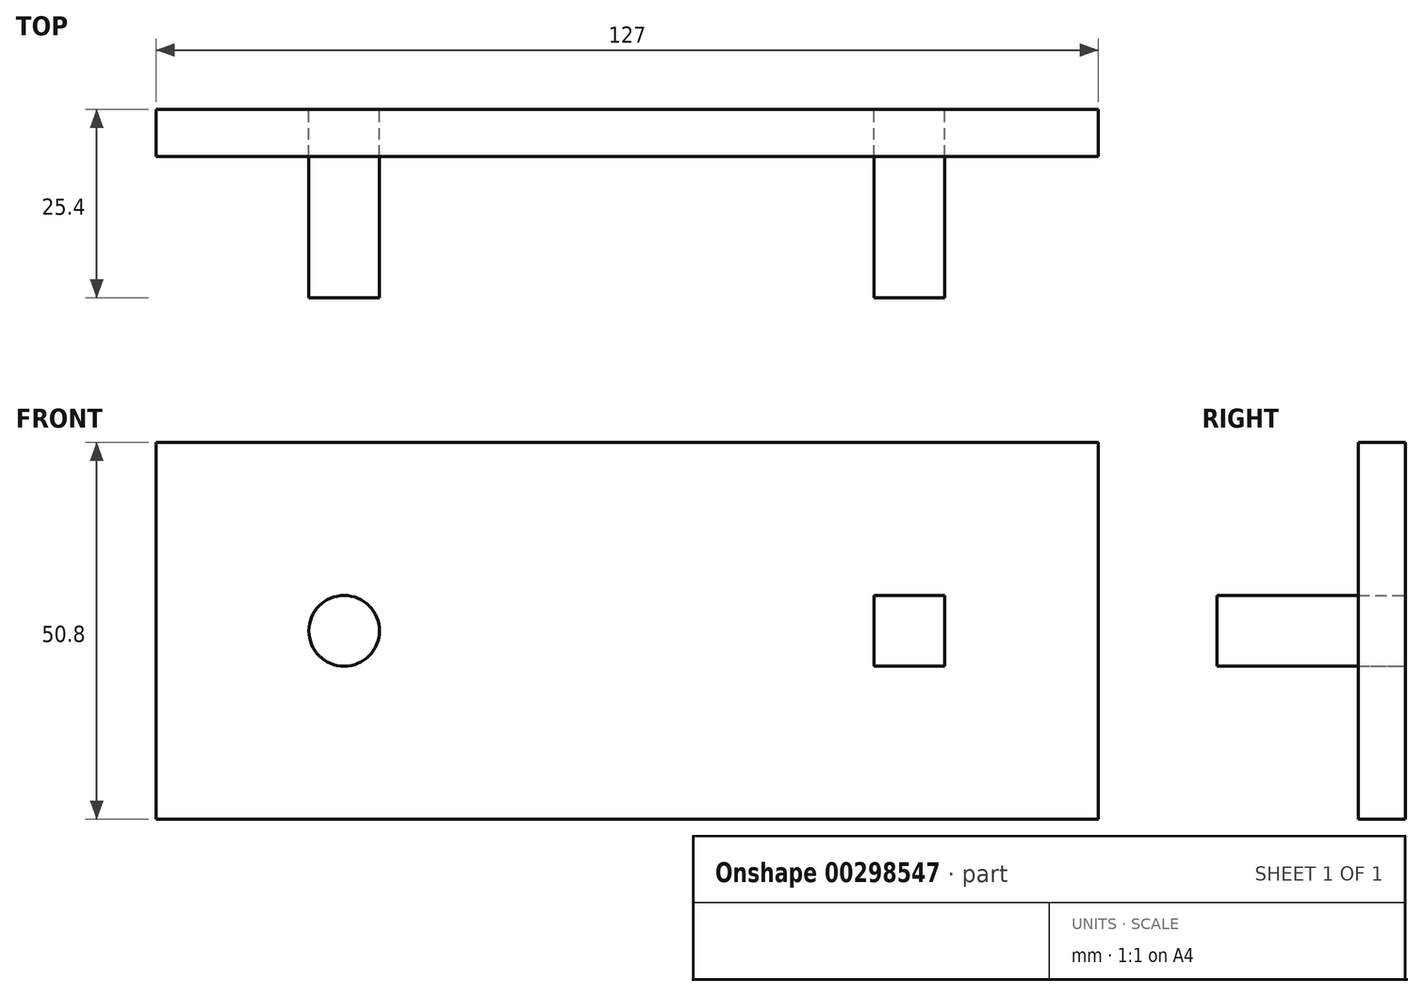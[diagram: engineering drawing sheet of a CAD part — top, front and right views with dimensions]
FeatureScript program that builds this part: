
annotation { "Feature Type Name" : "Feature", "Feature Type Description" : "" }
export const myFeature = defineFeature(function(context is Context, id is Id, definition is map)
    precondition{}
    {
        {
            var Q0;
            Q0=qCreatedBy(makeId("Front.planeOp"),FACE);
            var sketch = newSketch(context, id + "F0", { "sketchPlane" : qUnion([Q0])});
            skLineSegment(sketch, "E0.bottom", {"start": v(63.5, 25.4) * mm, "end": v(-63.5, 25.4) * mm});
            skLineSegment(sketch, "E0.top", {"start": v(63.5, -25.4) * mm, "end": v(-63.5, -25.4) * mm});
            skLineSegment(sketch, "E0.left", {"start": v(63.5, 25.4) * mm, "end": v(63.5, -25.4) * mm});
            skLineSegment(sketch, "E0.right", {"start": v(-63.5, 25.4) * mm, "end": v(-63.5, -25.4) * mm});
            skPoint(sketch, "E0.middle", {"position": v(0, 0) * mm});
            skSolve(sketch);
        }
        {
            var Q0;
            Q0=qCreatedBy(makeId("Front.planeOp"),FACE);
            var sketch = newSketch(context, id + "F1", { "sketchPlane" : qUnion([Q0])});
            skCircle(sketch, "E1", {"center": v(-38.15, 0) * mm, "radius": 4.76 * mm});
            skLineSegment(sketch, "E2.bottom", {"start": v(42.81, 4.76) * mm, "end": v(33.29, 4.76) * mm});
            skLineSegment(sketch, "E2.top", {"start": v(42.81, -4.76) * mm, "end": v(33.29, -4.76) * mm});
            skLineSegment(sketch, "E2.left", {"start": v(42.81, 4.76) * mm, "end": v(42.81, -4.76) * mm});
            skLineSegment(sketch, "E2.right", {"start": v(33.29, 4.76) * mm, "end": v(33.29, -4.76) * mm});
            skPoint(sketch, "E2.middle", {"position": v(38.05, 0) * mm});
            skSolve(sketch);
        }
        {
            var Q0;
            {var subQ0=sQuery(id+"F1.wireOp",EDGE,"5Zl7hWcx-Vfif-6HsS-f2ZM-u7ULnNQ5xVKX");var subQ1=sQuery(id+"F1.wireOp",EDGE,"ShflypP2-Z43F-BW97-jndV-6qC142foT7Cp");var subQ2=makeQuery(id+"F1.imprint","INTERSECT",VERTEX,{"derivedFrom":[subQ1,subQ0]});Q0=makeQuery(id+"F1.imprint","IMPRINT",FACE,{"disambiguationData":[TD([[makeQuery(id+"F1.imprint","IMPRINT",EDGE,{"disambiguationData":[TD([[subQ2,1.0]])],"derivedFrom":subQ1}),-1.0]])]});}
            var Q1;
            {var subQ0=sQuery(id+"F1.wireOp",EDGE,"5Zl7hWcx-Vfif-6HsS-f2ZM-u7ULnNQ5xVKX");var subQ1=sQuery(id+"F1.wireOp",EDGE,"ShflypP2-Z43F-BW97-jndV-6qC142foT7Cp");var subQ2=makeQuery(id+"F1.imprint","INTERSECT",VERTEX,{"derivedFrom":[subQ1,subQ0]});Q1=makeQuery(id+"F1.imprint","IMPRINT",FACE,{"disambiguationData":[TD([[makeQuery(id+"F1.imprint","IMPRINT",EDGE,{"disambiguationData":[TD([[subQ2,1.0]])],"derivedFrom":subQ1}),1.0]])]});}
            var Q2;
            {var subQ1=sQuery(id+"F1.wireOp",EDGE,"E2.bottom");Q2=makeQuery(id+"F1.imprint","IMPRINT",FACE,{"disambiguationData":[TD([[makeQuery(id+"F1.imprint","IMPRINT",EDGE,{"derivedFrom":subQ1}),1.0]])]});}
            var Q3;
            Q3=makeQuery(id+"F0.imprint","IMPRINT",FACE,{"disambiguationData":[TD([[makeQuery(id+"F0.imprint","IMPRINT",EDGE,{"derivedFrom":sQuery(id+"F0.wireOp",EDGE,"E0.bottom")}),1.0]])]});
            extrude(context, id + "F2", {"entities" : qUnion([Q0, Q1, Q2, Q3]), "depth" : 6.35 * mm});
        }
        {
            var Q0;
            Q0=qSketchRegion(id+"F1",true);
            extrude(context, id + "F3", {"entities" : qUnion([Q0]), "depth" : 25.4 * mm});
        }
    });
